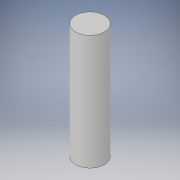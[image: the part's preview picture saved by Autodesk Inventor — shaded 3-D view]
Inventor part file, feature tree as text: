
AUTODESK INVENTOR PART (.ipt)
format: ipt  version: 2019 (Build 230136000, 136)  size: 89,088 bytes
history: native  units: in
note: dims shown in document units (in); Inventor stores cm internally (conversion verified against a paired STEP export)
features: extrude x1, sketch x1
ambient origin geometry x8: Origin, YZ Plane, XZ Plane, XY Plane, X Axis, Y Axis, Z Axis, Center Point
bodies: Solid1 (feature_tree)
feature tree (2):
  extrude  "Extrusion1"  Depth=1.0in TaperAngle=0.0deg
  sketch  "Sketch1"  dims[d0=0.25in d1=1.0in d2=0.0in]
